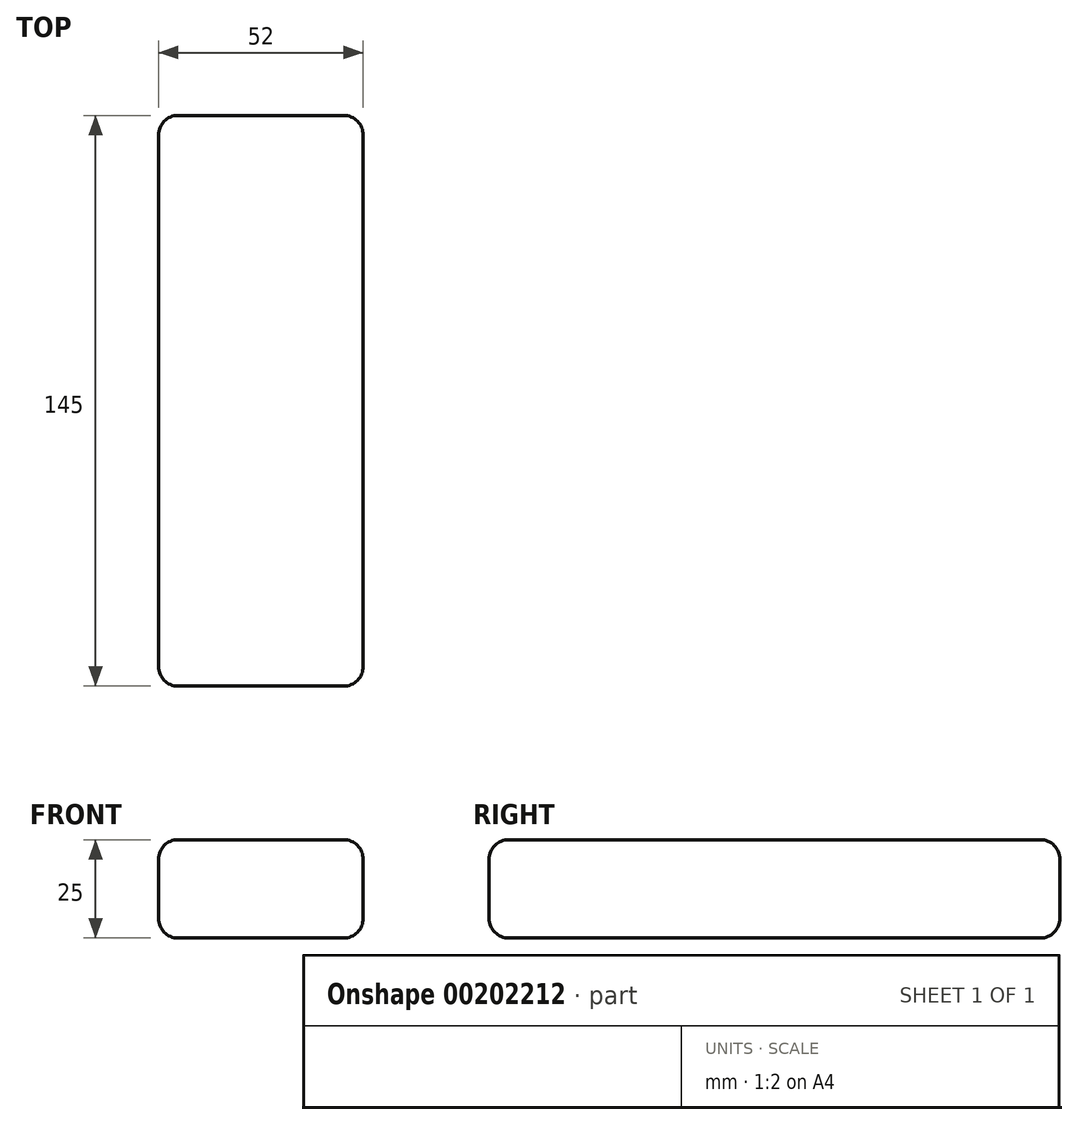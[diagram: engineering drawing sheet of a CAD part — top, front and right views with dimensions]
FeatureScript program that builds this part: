
annotation { "Feature Type Name" : "Feature", "Feature Type Description" : "" }
export const myFeature = defineFeature(function(context is Context, id is Id, definition is map)
    precondition{}
    {
        {
            var Q0;
            Q0=qCreatedBy(makeId("Top.planeOp"),FACE);
            var sketch = newSketch(context, id + "F0", { "sketchPlane" : qUnion([Q0])});
            skLineSegment(sketch, "E0.bottom", {"start": v(21, 72.5) * mm, "end": v(-21, 72.5) * mm});
            skLineSegment(sketch, "E0.top", {"start": v(21, -72.5) * mm, "end": v(-21, -72.5) * mm});
            skLineSegment(sketch, "E0.left", {"start": v(26, 67.5) * mm, "end": v(26, -67.5) * mm});
            skLineSegment(sketch, "E0.right", {"start": v(-26, 67.5) * mm, "end": v(-26, -67.5) * mm});
            skPoint(sketch, "E0.middle", {"position": v(0, 0) * mm});
            skPoint(sketch, "E1.visualSharp", {"position": v(-26, 72.5) * mm});
            skArc(sketch, "E1.filletArc", {"start": v(-21, 72.5) * mm, "mid": v(-24.54, 71.04) * mm, "end": v(-26, 67.5) * mm});
            skPoint(sketch, "E2.visualSharp", {"position": v(26, 72.5) * mm});
            skArc(sketch, "E2.filletArc", {"start": v(26, 67.5) * mm, "mid": v(24.54, 71.04) * mm, "end": v(21, 72.5) * mm});
            skPoint(sketch, "E3.visualSharp", {"position": v(-26, -72.5) * mm});
            skArc(sketch, "E3.filletArc", {"start": v(-26, -67.5) * mm, "mid": v(-24.54, -71.04) * mm, "end": v(-21, -72.5) * mm});
            skPoint(sketch, "E4.visualSharp", {"position": v(26, -72.5) * mm});
            skArc(sketch, "E4.filletArc", {"start": v(21, -72.5) * mm, "mid": v(24.54, -71.04) * mm, "end": v(26, -67.5) * mm});
            skSolve(sketch);
        }
        {
            var Q0;
            Q0=qSketchRegion(id+"F0",true);
            extrude(context, id + "F1", {"entities" : qUnion([Q0]), "depth" : 25 * mm});
        }
        {
            var Q0;
            Q0=makeQuery(id+"F1.opExtrude","CAP_FACE",FACE,{"disambiguationData":[OSD([sQuery(id+"F0.wireOp",EDGE,"E0.bottom"),sQuery(id+"F0.wireOp",EDGE,"E0.top"),sQuery(id+"F0.wireOp",EDGE,"E0.left"),sQuery(id+"F0.wireOp",EDGE,"E0.right"),sQuery(id+"F0.wireOp",EDGE,"E1.filletArc"),sQuery(id+"F0.wireOp",EDGE,"E2.filletArc"),sQuery(id+"F0.wireOp",EDGE,"E3.filletArc"),sQuery(id+"F0.wireOp",EDGE,"E4.filletArc")])],"isStart":false});
            var Q1;
            Q1=makeQuery(id+"F1.opExtrude","CAP_FACE",FACE,{"disambiguationData":[OSD([sQuery(id+"F0.wireOp",EDGE,"E0.bottom"),sQuery(id+"F0.wireOp",EDGE,"E0.top"),sQuery(id+"F0.wireOp",EDGE,"E0.left"),sQuery(id+"F0.wireOp",EDGE,"E0.right"),sQuery(id+"F0.wireOp",EDGE,"E1.filletArc"),sQuery(id+"F0.wireOp",EDGE,"E2.filletArc"),sQuery(id+"F0.wireOp",EDGE,"E3.filletArc"),sQuery(id+"F0.wireOp",EDGE,"E4.filletArc")])],"isStart":true});
            fillet(context, id + "F2", {"entities" : qUnion([Q0, Q1]), "radius" : 5 * mm, "tangentPropagation" : true, "allowEdgeOverflow" : false});
        }
    });
